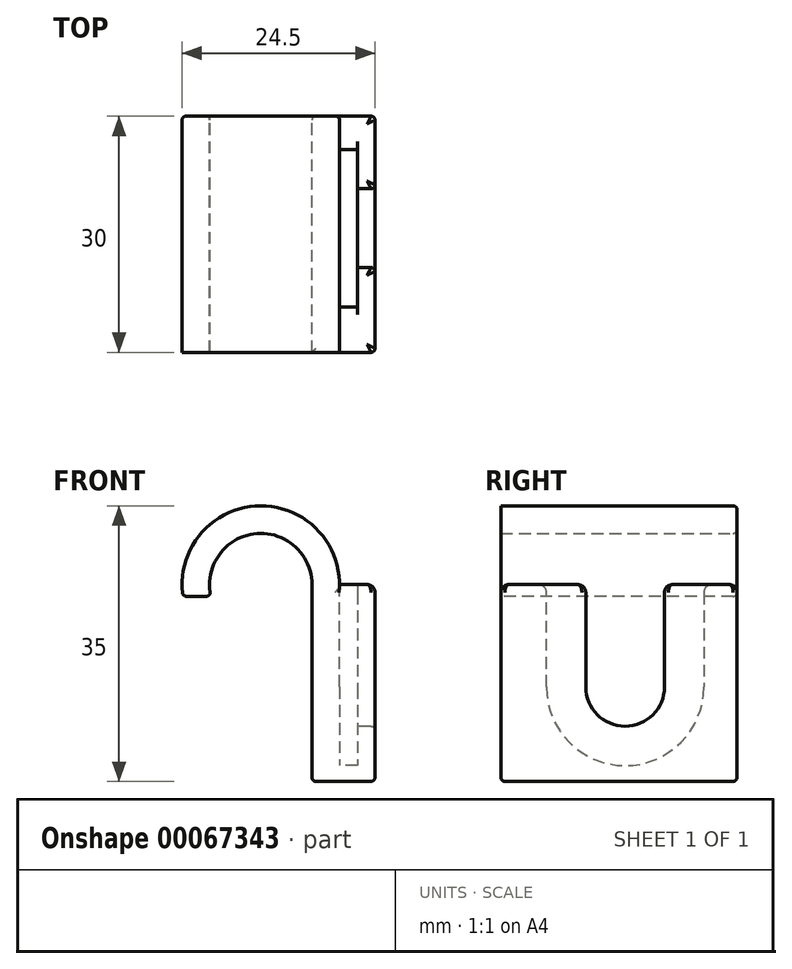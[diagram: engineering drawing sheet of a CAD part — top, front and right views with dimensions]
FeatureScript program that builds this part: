
annotation { "Feature Type Name" : "Feature", "Feature Type Description" : "" }
export const myFeature = defineFeature(function(context is Context, id is Id, definition is map)
    precondition{}
    {
        {
            var Q0;
            Q0=qCreatedBy(makeId("Top.planeOp"),FACE);
            var sketch = newSketch(context, id + "F0", { "sketchPlane" : qUnion([Q0])});
            skLineSegment(sketch, "E0.bottom", {"start": v(0.36, -15.78) * mm, "end": v(8.36, -15.78) * mm});
            skLineSegment(sketch, "E0.top", {"start": v(0.36, 14.22) * mm, "end": v(8.36, 14.22) * mm});
            skLineSegment(sketch, "E0.left", {"start": v(0.36, -15.78) * mm, "end": v(0.36, 14.22) * mm});
            skLineSegment(sketch, "E0.right", {"start": v(8.36, -15.78) * mm, "end": v(8.36, 14.22) * mm});
            skSolve(sketch);
        }
        {
            var Q0;
            Q0=makeQuery(id+"F0.imprint","IMPRINT",FACE,{"disambiguationData":[TD([[makeQuery(id+"F0.imprint","IMPRINT",EDGE,{"derivedFrom":sQuery(id+"F0.wireOp",EDGE,"E0.bottom")}),1.0]])]});
            extrude(context, id + "F1", {"entities" : qUnion([Q0]), "depth" : 25 * mm});
        }
        {
            var Q0;
            Q0=makeQuery(id+"F1.opExtrude","SWEPT_FACE",FACE,{"disambiguationData":[OSD([sQuery(id+"F0.wireOp",EDGE,"E0.right")])]});
            cPlane(context, id + "F2", {"entities" : qUnion([Q0]), "cplaneType" : CPlaneType.OFFSET, "offset" : 4.5 * mm, "oppositeDirection" : true, "width" : 150 * mm, "height" : 150 * mm});
        }
        {
            var Q0;
            Q0=makeQuery(id+"F1.opExtrude","SWEPT_FACE",FACE,{"disambiguationData":[OSD([sQuery(id+"F0.wireOp",EDGE,"E0.right")])]});
            cPlane(context, id + "F3", {"entities" : qUnion([Q0]), "cplaneType" : CPlaneType.OFFSET, "offset" : 2.25 * mm, "oppositeDirection" : true, "width" : 150 * mm, "height" : 150 * mm});
        }
        {
            var Q0;
            Q0=qCreatedBy(id+"F2.planeOp",FACE);
            var sketch = newSketch(context, id + "F4", { "sketchPlane" : qUnion([Q0])});
            skArc(sketch, "E1", {"start": v(-10, 12) * mm, "mid": v(0, 2) * mm, "end": v(10, 12) * mm});
            skLineSegment(sketch, "E2", {"start": v(0, 12) * mm, "end": v(-10, 12) * mm, "construction": true});
            skLineSegment(sketch, "E3", {"start": v(0, 12) * mm, "end": v(10, 12) * mm, "construction": true});
            skLineSegment(sketch, "E4", {"start": v(-10, 12) * mm, "end": v(-10, 26.3) * mm});
            skLineSegment(sketch, "E5", {"start": v(-10, 26.3) * mm, "end": v(10, 26.3) * mm});
            skLineSegment(sketch, "E6", {"start": v(10, 26.3) * mm, "end": v(10, 12) * mm});
            skSolve(sketch);
        }
        {
            var Q0;
            Q0 = qSketchRegion(id + "F4", true);
            var Q1;
            Q1=qCreatedBy(id+"F3.planeOp",FACE);
            extrude(context, id + "F5", {"entities" : qUnion([Q0]), "operationType" : NewBodyOperationType.REMOVE, "endBound" : BoundingType.UP_TO_SURFACE, "endBoundEntityFace" : qUnion([Q1]), "depth" : 1.65 * mm});
        }
        {
            var Q0;
            Q0=qCreatedBy(id+"F3.planeOp",FACE);
            var sketch = newSketch(context, id + "F6", { "sketchPlane" : qUnion([Q0])});
            skArc(sketch, "E7", {"start": v(-5, 12) * mm, "mid": v(0, 7) * mm, "end": v(5, 12) * mm});
            skLineSegment(sketch, "E8", {"start": v(0, 12) * mm, "end": v(-5, 12) * mm, "construction": true});
            skLineSegment(sketch, "E9", {"start": v(0, 12) * mm, "end": v(5, 12) * mm, "construction": true});
            skLineSegment(sketch, "E10", {"start": v(-5, 12) * mm, "end": v(-5, 26.87) * mm});
            skLineSegment(sketch, "E11", {"start": v(5, 12) * mm, "end": v(5, 26.87) * mm});
            skLineSegment(sketch, "E12", {"start": v(5, 26.87) * mm, "end": v(-5, 26.87) * mm});
            skSolve(sketch);
        }
        {
            var Q0;
            Q0 = qSketchRegion(id + "F6", true);
            extrude(context, id + "F7", {"entities" : qUnion([Q0]), "operationType" : NewBodyOperationType.REMOVE, "endBound" : BoundingType.THROUGH_ALL, "depth" : 25 * mm});
        }
        {
            var Q0;
            Q0=makeQuery(id+"F1.opExtrude","SWEPT_FACE",FACE,{"disambiguationData":[OSD([sQuery(id+"F0.wireOp",EDGE,"E0.top")])]});
            var sketch = newSketch(context, id + "F8", { "sketchPlane" : qUnion([Q0])});
            skArc(sketch, "E13", {"start": v(12.46, 23.5) * mm, "mid": v(6.9, 31.46) * mm, "end": v(-0.36, 25) * mm});
            skArc(sketch, "E14", {"start": v(16.02, 23.5) * mm, "mid": v(6.89, 34.97) * mm, "end": v(-3.86, 25) * mm});
            skLineSegment(sketch, "E15", {"start": v(12.46, 23.5) * mm, "end": v(16.02, 23.5) * mm});
            skPoint(sketch, "E16", {"position": v(-3.86, 25) * mm});
            skSolve(sketch);
        }
        {
            var Q0;
            {var subQ0=sQuery(id+"F8.wireOp",EDGE,"E13");Q0=makeQuery(id+"F8.imprint","IMPRINT",FACE,{"disambiguationData":[TD([[makeQuery(id+"F8.imprint","IMPRINT",EDGE,{"derivedFrom":subQ0}),-1.0]])]});}
            var Q1;
            Q1=makeQuery(id+"F1.opExtrude","SWEPT_FACE",FACE,{"disambiguationData":[OSD([sQuery(id+"F0.wireOp",EDGE,"E0.bottom")])]});
            extrude(context, id + "F9", {"entities" : qUnion([Q0]), "operationType" : NewBodyOperationType.ADD, "endBound" : BoundingType.UP_TO_SURFACE, "oppositeDirection" : true, "endBoundEntityFace" : qUnion([Q1]), "depth" : 25 * mm});
        }
        {
            var Q0;
            Q0=makeQuery(id+"F7.boolean.opBoolean","INTERSECT",EDGE,{"derivedFrom":[makeQuery(id+"F1.opExtrude","CAP_FACE",FACE,{"disambiguationData":[OSD([sQuery(id+"F0.wireOp",EDGE,"E0.bottom"),sQuery(id+"F0.wireOp",EDGE,"E0.top"),sQuery(id+"F0.wireOp",EDGE,"E0.left"),sQuery(id+"F0.wireOp",EDGE,"E0.right")])],"isStart":false}),makeQuery(id+"F7.opExtrude","SWEPT_FACE",FACE,{"disambiguationData":[OSD([sQuery(id+"F6.wireOp",EDGE,"E10")])]})]});
            var Q1;
            Q1=makeQuery(id+"F7.boolean.opBoolean","INTERSECT",EDGE,{"derivedFrom":[makeQuery(id+"F1.opExtrude","CAP_FACE",FACE,{"disambiguationData":[OSD([sQuery(id+"F0.wireOp",EDGE,"E0.bottom"),sQuery(id+"F0.wireOp",EDGE,"E0.top"),sQuery(id+"F0.wireOp",EDGE,"E0.left"),sQuery(id+"F0.wireOp",EDGE,"E0.right")])],"isStart":false}),makeQuery(id+"F7.opExtrude","SWEPT_FACE",FACE,{"disambiguationData":[OSD([sQuery(id+"F6.wireOp",EDGE,"E11")])]})]});
            var Q2;
            Q2=makeQuery(id+"F5.boolean.opBoolean","INTERSECT",EDGE,{"derivedFrom":[makeQuery(id+"F1.opExtrude","CAP_FACE",FACE,{"disambiguationData":[OSD([sQuery(id+"F0.wireOp",EDGE,"E0.bottom"),sQuery(id+"F0.wireOp",EDGE,"E0.top"),sQuery(id+"F0.wireOp",EDGE,"E0.left"),sQuery(id+"F0.wireOp",EDGE,"E0.right")])],"isStart":false}),makeQuery(id+"F5.opExtrude","SWEPT_FACE",FACE,{"disambiguationData":[OSD([sQuery(id+"F4.wireOp",EDGE,"E6")])]})]});
            var Q3;
            Q3=makeQuery(id+"F5.boolean.opBoolean","INTERSECT",EDGE,{"derivedFrom":[makeQuery(id+"F1.opExtrude","CAP_FACE",FACE,{"disambiguationData":[OSD([sQuery(id+"F0.wireOp",EDGE,"E0.bottom"),sQuery(id+"F0.wireOp",EDGE,"E0.top"),sQuery(id+"F0.wireOp",EDGE,"E0.left"),sQuery(id+"F0.wireOp",EDGE,"E0.right")])],"isStart":false}),makeQuery(id+"F5.opExtrude","SWEPT_FACE",FACE,{"disambiguationData":[OSD([sQuery(id+"F4.wireOp",EDGE,"E4")])]})]});
            var Q4;
            {var subQ0=makeQuery(id+"F1.opExtrude","CAP_FACE",FACE,{"disambiguationData":[OSD([sQuery(id+"F0.wireOp",EDGE,"E0.bottom"),sQuery(id+"F0.wireOp",EDGE,"E0.top"),sQuery(id+"F0.wireOp",EDGE,"E0.left"),sQuery(id+"F0.wireOp",EDGE,"E0.right")])],"isStart":false});var subQ1=makeQuery(id+"F5.opExtrude","CAP_FACE",FACE,{"disambiguationData":[OSD([dummyQuery(id+"F3.planeOp",FACE)])],"isStart":false});Q4=makeQuery(id+"F7.boolean.opBoolean","SPLIT",EDGE,{"disambiguationData":[TD([makeQuery(id+"F5.boolean.opBoolean","COPY",FACE,{"derivedFrom":makeQuery(id+"F5.opExtrude","SWEPT_FACE",FACE,{"disambiguationData":[OSD([sQuery(id+"F4.wireOp",EDGE,"E4")])]})})])],"derivedFrom":makeQuery(id+"F5.boolean.opBoolean","INTERSECT",EDGE,{"derivedFrom":[subQ0,subQ1]})});}
            var Q5;
            {var subQ0=makeQuery(id+"F1.opExtrude","CAP_FACE",FACE,{"disambiguationData":[OSD([sQuery(id+"F0.wireOp",EDGE,"E0.bottom"),sQuery(id+"F0.wireOp",EDGE,"E0.top"),sQuery(id+"F0.wireOp",EDGE,"E0.left"),sQuery(id+"F0.wireOp",EDGE,"E0.right")])],"isStart":false});var subQ1=makeQuery(id+"F5.opExtrude","CAP_FACE",FACE,{"disambiguationData":[OSD([dummyQuery(id+"F3.planeOp",FACE)])],"isStart":false});Q5=makeQuery(id+"F7.boolean.opBoolean","SPLIT",EDGE,{"disambiguationData":[TD([makeQuery(id+"F5.boolean.opBoolean","COPY",FACE,{"derivedFrom":makeQuery(id+"F5.opExtrude","SWEPT_FACE",FACE,{"disambiguationData":[OSD([sQuery(id+"F4.wireOp",EDGE,"E6")])]})})])],"derivedFrom":makeQuery(id+"F5.boolean.opBoolean","INTERSECT",EDGE,{"derivedFrom":[subQ0,subQ1]})});}
            var Q6;
            {var subQ0=sQuery(id+"F0.wireOp",EDGE,"E0.right");var subQ1=sQuery(id+"F0.wireOp",EDGE,"E0.top");Q6=makeQuery(id+"F7.boolean.opBoolean","SPLIT",EDGE,{"disambiguationData":[TD([makeQuery(id+"F1.opExtrude","SWEPT_FACE",FACE,{"disambiguationData":[OSD([subQ1])]})])],"derivedFrom":makeQuery(id+"F1.opExtrude","CAP_EDGE",EDGE,{"disambiguationData":[OSD([subQ0])],"isStart":false})});}
            var Q7;
            Q7=makeQuery(id+"F1.opExtrude","CAP_EDGE",EDGE,{"disambiguationData":[OSD([sQuery(id+"F0.wireOp",EDGE,"E0.top")])],"isStart":false});
            var Q8;
            {var subQ0=sQuery(id+"F0.wireOp",EDGE,"E0.bottom");var subQ1=sQuery(id+"F0.wireOp",EDGE,"E0.right");Q8=makeQuery(id+"F7.boolean.opBoolean","SPLIT",EDGE,{"disambiguationData":[TD([makeQuery(id+"F1.opExtrude","SWEPT_FACE",FACE,{"disambiguationData":[OSD([subQ0])]})])],"derivedFrom":makeQuery(id+"F1.opExtrude","CAP_EDGE",EDGE,{"disambiguationData":[OSD([subQ1])],"isStart":false})});}
            var Q9;
            Q9=makeQuery(id+"F1.opExtrude","CAP_EDGE",EDGE,{"disambiguationData":[OSD([sQuery(id+"F0.wireOp",EDGE,"E0.bottom")])],"isStart":false});
            fillet(context, id + "F10", {"entities" : qUnion([Q0, Q1, Q2, Q3, Q4, Q5, Q6, Q7, Q8, Q9]), "radius" : 1 * mm, "tangentPropagation" : true, "allowEdgeOverflow" : false});
        }
        {
            var Q0;
            Q0=makeQuery(id+"F7.boolean.opBoolean","INTERSECT",EDGE,{"derivedFrom":[makeQuery(id+"F1.opExtrude","SWEPT_FACE",FACE,{"disambiguationData":[OSD([sQuery(id+"F0.wireOp",EDGE,"E0.right")])]}),makeQuery(id+"F7.opExtrude","SWEPT_FACE",FACE,{"disambiguationData":[OSD([sQuery(id+"F6.wireOp",EDGE,"E10")])]})]});
            var Q1;
            Q1=makeQuery(id+"F7.boolean.opBoolean","INTERSECT",EDGE,{"derivedFrom":[makeQuery(id+"F1.opExtrude","SWEPT_FACE",FACE,{"disambiguationData":[OSD([sQuery(id+"F0.wireOp",EDGE,"E0.right")])]}),makeQuery(id+"F7.opExtrude","SWEPT_FACE",FACE,{"disambiguationData":[OSD([sQuery(id+"F6.wireOp",EDGE,"E11")])]})]});
            var Q2;
            Q2=makeQuery(id+"F7.boolean.opBoolean","INTERSECT",EDGE,{"derivedFrom":[makeQuery(id+"F1.opExtrude","SWEPT_FACE",FACE,{"disambiguationData":[OSD([sQuery(id+"F0.wireOp",EDGE,"E0.right")])]}),makeQuery(id+"F7.opExtrude","SWEPT_FACE",FACE,{"disambiguationData":[OSD([sQuery(id+"F6.wireOp",EDGE,"E7")])]})]});
            var Q3;
            Q3=makeQuery(id+"F7.boolean.opBoolean","COPY",EDGE,{"derivedFrom":makeQuery(id+"F7.opExtrude","CAP_EDGE",EDGE,{"disambiguationData":[OSD([sQuery(id+"F6.wireOp",EDGE,"E7")])],"isStart":true})});
            var Q4;
            Q4=makeQuery(id+"F7.boolean.opBoolean","COPY",EDGE,{"derivedFrom":makeQuery(id+"F7.opExtrude","CAP_EDGE",EDGE,{"disambiguationData":[OSD([sQuery(id+"F6.wireOp",EDGE,"E11")])],"isStart":true})});
            var Q5;
            Q5=makeQuery(id+"F7.boolean.opBoolean","COPY",EDGE,{"derivedFrom":makeQuery(id+"F7.opExtrude","CAP_EDGE",EDGE,{"disambiguationData":[OSD([sQuery(id+"F6.wireOp",EDGE,"E10")])],"isStart":true})});
            fillet(context, id + "F11", {"entities" : qUnion([Q0, Q1, Q2, Q3, Q4, Q5]), "radius" : .5 * mm, "tangentPropagation" : true, "allowEdgeOverflow" : false});
        }
        {
            var Q0;
            Q0=makeQuery(id+"F9.opExtrude","TWEAK_EDGE",EDGE,{"derivedFrom":[makeQuery(id+"F1.opExtrude","SWEPT_FACE",FACE,{"disambiguationData":[OSD([sQuery(id+"F0.wireOp",EDGE,"E0.bottom")])]}),makeQuery(id+"F8.imprint","IMPRINT",EDGE,{"derivedFrom":sQuery(id+"F8.wireOp",EDGE,"E14")})]});
            var Q1;
            Q1=makeQuery(id+"F9.opExtrude","TWEAK_EDGE",EDGE,{"derivedFrom":[makeQuery(id+"F1.opExtrude","SWEPT_FACE",FACE,{"disambiguationData":[OSD([sQuery(id+"F0.wireOp",EDGE,"E0.bottom")])]}),makeQuery(id+"F8.imprint","IMPRINT",EDGE,{"derivedFrom":sQuery(id+"F8.wireOp",EDGE,"E13")})]});
            var Q2;
            Q2=makeQuery(id+"F9.opExtrude","TWEAK_EDGE",EDGE,{"derivedFrom":[makeQuery(id+"F1.opExtrude","SWEPT_FACE",FACE,{"disambiguationData":[OSD([sQuery(id+"F0.wireOp",EDGE,"E0.bottom")])]}),makeQuery(id+"F8.imprint","IMPRINT",EDGE,{"derivedFrom":sQuery(id+"F8.wireOp",EDGE,"E15")})]});
            var Q3;
            Q3=makeQuery(id+"F9.opExtrude","SWEPT_EDGE",EDGE,{"disambiguationData":[OSD([sQuery(id+"F8.wireOp",EDGE,"E14"),sQuery(id+"F8.wireOp",EDGE,"E15")])]});
            var Q4;
            Q4=makeQuery(id+"F9.opExtrude","SWEPT_EDGE",EDGE,{"disambiguationData":[OSD([sQuery(id+"F8.wireOp",EDGE,"E13"),sQuery(id+"F8.wireOp",EDGE,"E15")])]});
            var Q5;
            Q5=makeQuery(id+"F9.opExtrude","CAP_EDGE",EDGE,{"disambiguationData":[OSD([sQuery(id+"F8.wireOp",EDGE,"E15")])],"isStart":true});
            var Q6;
            Q6=makeQuery(id+"F9.opExtrude","CAP_EDGE",EDGE,{"disambiguationData":[OSD([sQuery(id+"F8.wireOp",EDGE,"E14")])],"isStart":true});
            var Q7;
            Q7=makeQuery(id+"F9.opExtrude","CAP_EDGE",EDGE,{"disambiguationData":[OSD([sQuery(id+"F8.wireOp",EDGE,"E13")])],"isStart":true});
            fillet(context, id + "F12", {"entities" : qUnion([Q0, Q1, Q2, Q3, Q4, Q5, Q6, Q7]), "radius" : .5 * mm, "tangentPropagation" : true, "allowEdgeOverflow" : false});
        }
        {
            var Q0;
            Q0=makeQuery(id+"F1.opExtrude","SWEPT_EDGE",EDGE,{"disambiguationData":[OSD([sQuery(id+"F0.wireOp",EDGE,"E0.top"),sQuery(id+"F0.wireOp",EDGE,"E0.right")])]});
            var Q1;
            Q1=makeQuery(id+"F1.opExtrude","SWEPT_EDGE",EDGE,{"disambiguationData":[OSD([sQuery(id+"F0.wireOp",EDGE,"E0.bottom"),sQuery(id+"F0.wireOp",EDGE,"E0.right")])]});
            var Q2;
            Q2=makeQuery(id+"F1.opExtrude","CAP_EDGE",EDGE,{"disambiguationData":[OSD([sQuery(id+"F0.wireOp",EDGE,"E0.left")])],"isStart":true});
            var Q3;
            Q3=makeQuery(id+"F1.opExtrude","CAP_EDGE",EDGE,{"disambiguationData":[OSD([sQuery(id+"F0.wireOp",EDGE,"E0.bottom")])],"isStart":true});
            var Q4;
            Q4=makeQuery(id+"F1.opExtrude","CAP_EDGE",EDGE,{"disambiguationData":[OSD([sQuery(id+"F0.wireOp",EDGE,"E0.right")])],"isStart":true});
            var Q5;
            Q5=makeQuery(id+"F1.opExtrude","CAP_EDGE",EDGE,{"disambiguationData":[OSD([sQuery(id+"F0.wireOp",EDGE,"E0.top")])],"isStart":true});
            fillet(context, id + "F13", {"entities" : qUnion([Q0, Q1, Q2, Q3, Q4, Q5]), "radius" : .5 * mm, "tangentPropagation" : true, "allowEdgeOverflow" : false});
        }
    });
